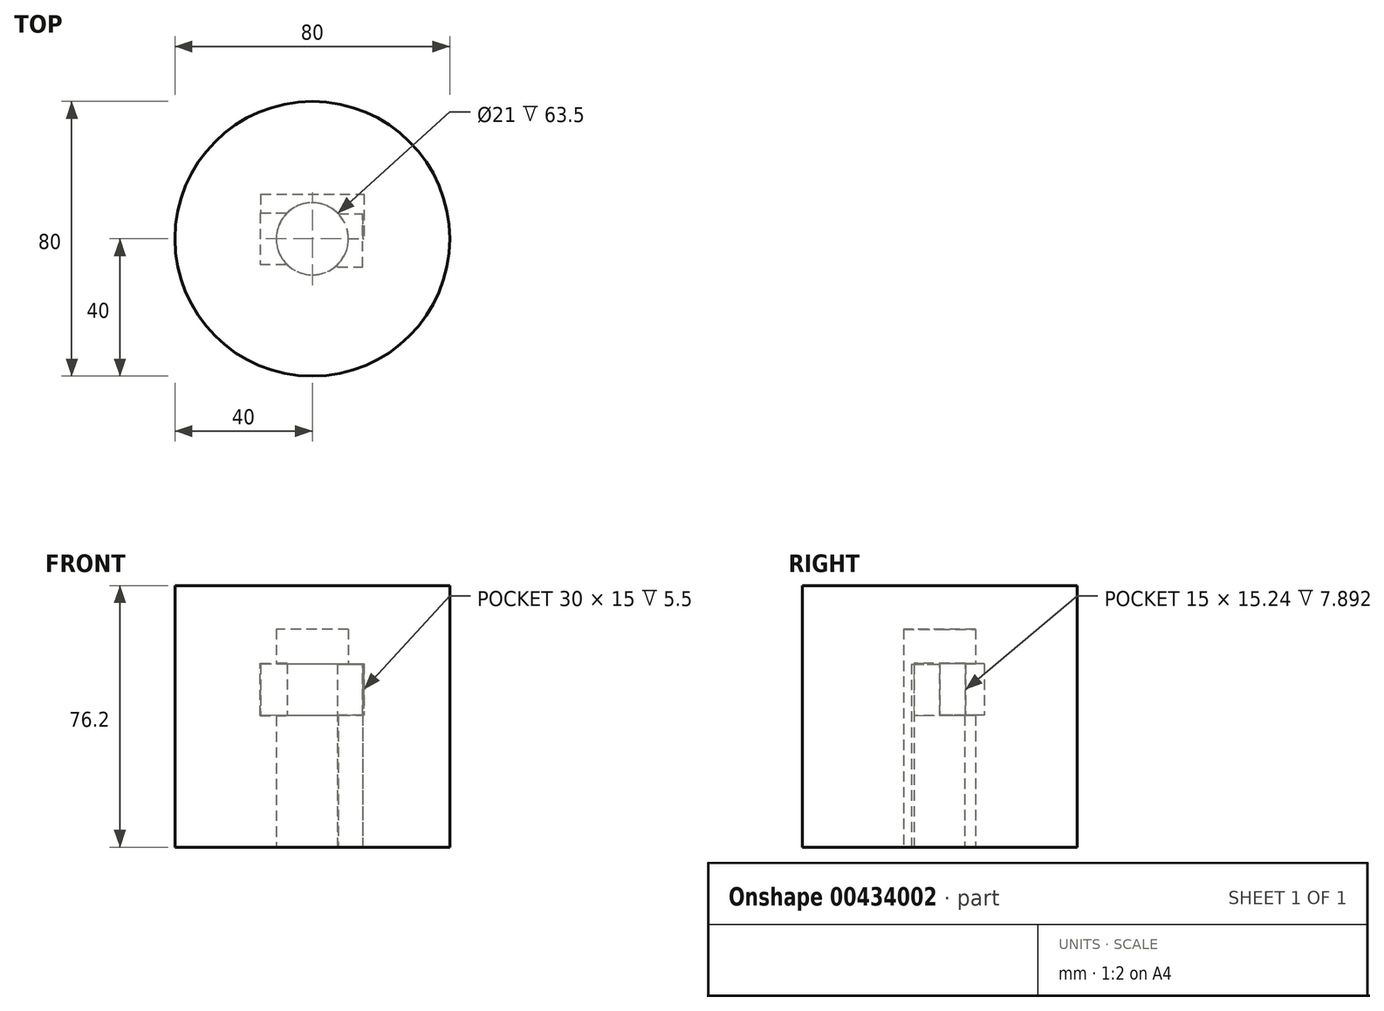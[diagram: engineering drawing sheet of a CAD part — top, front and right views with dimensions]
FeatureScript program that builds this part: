
annotation { "Feature Type Name" : "Feature", "Feature Type Description" : "" }
export const myFeature = defineFeature(function(context is Context, id is Id, definition is map)
    precondition{}
    {
        {
            var Q0;
            Q0=qCreatedBy(makeId("Top.planeOp"),FACE);
            var sketch = newSketch(context, id + "F0", { "sketchPlane" : qUnion([Q0])});
            skCircle(sketch, "E0", {"center": v(0, 0) * mm, "radius": 40 * mm});
            skSolve(sketch);
        }
        {
            var Q0;
            Q0 = qSketchRegion(id + "F0", true);
            extrude(context, id + "F1", {"entities" : qUnion([Q0]), "depth" : 76.2 * mm});
        }
        {
            var Q0;
            Q0=qCreatedBy(makeId("Top.planeOp"),FACE);
            var sketch = newSketch(context, id + "F2", { "sketchPlane" : qUnion([Q0])});
            skCircle(sketch, "E1", {"center": v(0, 0) * mm, "radius": 10.5 * mm});
            skSolve(sketch);
        }
        {
            var Q0;
            Q0 = qSketchRegion(id + "F2", true);
            extrude(context, id + "F3", {"entities" : qUnion([Q0]), "operationType" : NewBodyOperationType.REMOVE, "depth" : 63.5 * mm});
        }
        {
            var Q0;
            Q0=qCreatedBy(makeId("Top.planeOp"),FACE);
            var sketch = newSketch(context, id + "F4", { "sketchPlane" : qUnion([Q0])});
            skLineSegment(sketch, "E2.bottom", {"start": v(7.35, -8.25) * mm, "end": v(14.7, -8.25) * mm});
            skLineSegment(sketch, "E2.top", {"start": v(7.35, 7.25) * mm, "end": v(14.7, 7.25) * mm});
            skLineSegment(sketch, "E2.left", {"start": v(7.35, -8.25) * mm, "end": v(7.35, 7.25) * mm});
            skLineSegment(sketch, "E2.right", {"start": v(14.7, -8.25) * mm, "end": v(14.7, 7.25) * mm});
            skSolve(sketch);
        }
        {
            var Q0;
            Q0 = qSketchRegion(id + "F4", true);
            extrude(context, id + "F5", {"entities" : qUnion([Q0]), "operationType" : NewBodyOperationType.REMOVE, "depth" : 53.34 * mm});
        }
        {
            var Q0;
            Q0=qCreatedBy(makeId("Top.planeOp"),FACE);
            cPlane(context, id + "F6", {"entities" : qUnion([Q0]), "cplaneType" : CPlaneType.OFFSET, "offset" : 53.5 * mm, "width" : 152.4 * mm, "height" : 152.4 * mm});
        }
        {
            var Q0;
            Q0=qCreatedBy(id+"F6.planeOp",FACE);
            var sketch = newSketch(context, id + "F7", { "sketchPlane" : qUnion([Q0])});
            skLineSegment(sketch, "E3.bottom", {"start": v(-15.24, 7.5) * mm, "end": v(0, 7.5) * mm});
            skLineSegment(sketch, "E3.top", {"start": v(-15.24, -7.5) * mm, "end": v(0, -7.5) * mm});
            skLineSegment(sketch, "E3.left", {"start": v(-15.24, 7.5) * mm, "end": v(-15.24, -7.5) * mm});
            skLineSegment(sketch, "E3.right", {"start": v(0, 7.5) * mm, "end": v(0, -7.5) * mm});
            skSolve(sketch);
        }
        {
            var Q0;
            Q0 = qSketchRegion(id + "F7", true);
            extrude(context, id + "F8", {"entities" : qUnion([Q0]), "operationType" : NewBodyOperationType.REMOVE, "oppositeDirection" : true, "depth" : 15.24 * mm});
        }
        {
            var Q0;
            Q0=qCreatedBy(makeId("Front.planeOp"),FACE);
            var sketch = newSketch(context, id + "F9", { "sketchPlane" : qUnion([Q0])});
            skLineSegment(sketch, "E4.bottom", {"start": v(-15, 53.42) * mm, "end": v(15, 53.42) * mm});
            skLineSegment(sketch, "E4.top", {"start": v(-15, 38.42) * mm, "end": v(15, 38.42) * mm});
            skLineSegment(sketch, "E4.left", {"start": v(-15, 53.42) * mm, "end": v(-15, 38.42) * mm});
            skLineSegment(sketch, "E4.right", {"start": v(15, 53.42) * mm, "end": v(15, 38.42) * mm});
            skSolve(sketch);
        }
        {
            var Q0;
            Q0 = qSketchRegion(id + "F9", true);
            extrude(context, id + "F10", {"entities" : qUnion([Q0]), "operationType" : NewBodyOperationType.REMOVE, "oppositeDirection" : true, "depth" : 13 * mm});
        }
    });
